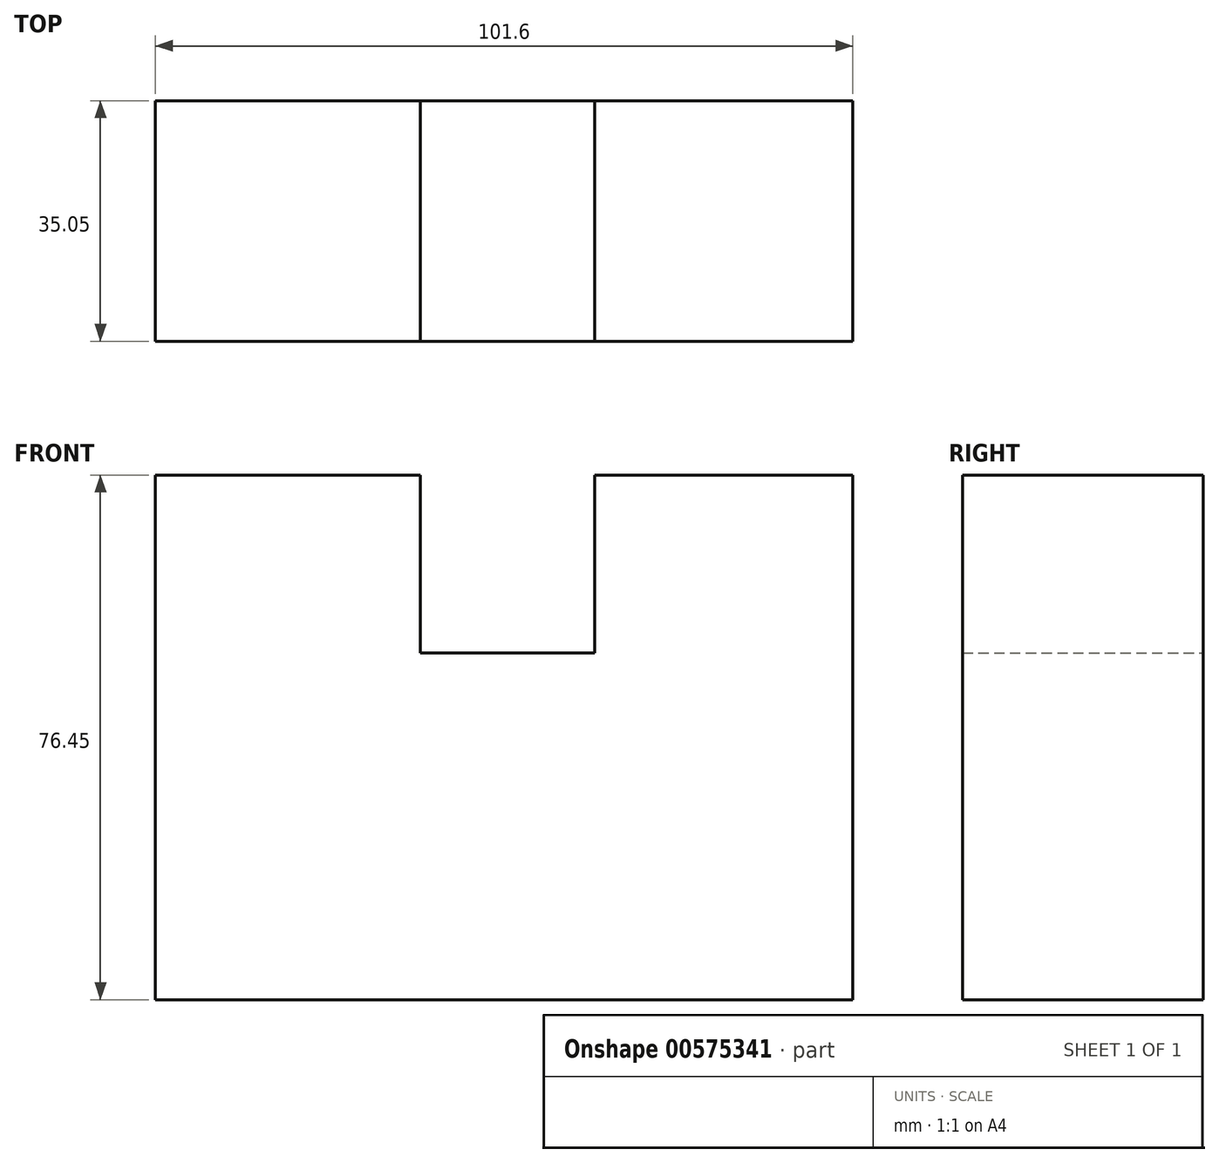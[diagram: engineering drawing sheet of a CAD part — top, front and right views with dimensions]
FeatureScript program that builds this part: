
annotation { "Feature Type Name" : "Feature", "Feature Type Description" : "" }
export const myFeature = defineFeature(function(context is Context, id is Id, definition is map)
    precondition{}
    {
        {
            var Q0;
            Q0=qCreatedBy(makeId("Front.planeOp"),FACE);
            var sketch = newSketch(context, id + "F0", { "sketchPlane" : qUnion([Q0])});
            skLineSegment(sketch, "E0", {"start": v(0, 0) * mm, "end": v(101.6, 0) * mm});
            skLineSegment(sketch, "E1", {"start": v(101.6, 0) * mm, "end": v(101.6, 76.45) * mm});
            skLineSegment(sketch, "E2", {"start": v(101.6, 76.45) * mm, "end": v(64, 76.45) * mm});
            skLineSegment(sketch, "E3", {"start": v(64, 76.45) * mm, "end": v(64, 50.55) * mm});
            skLineSegment(sketch, "E4", {"start": v(64, 50.55) * mm, "end": v(38.6, 50.55) * mm});
            skLineSegment(sketch, "E5", {"start": v(38.6, 50.55) * mm, "end": v(38.6, 76.45) * mm});
            skLineSegment(sketch, "E6", {"start": v(38.6, 76.45) * mm, "end": v(0, 76.45) * mm});
            skLineSegment(sketch, "E7", {"start": v(0, 76.45) * mm, "end": v(0, 0) * mm});
            skSolve(sketch);
        }
        {
            var Q0;
            Q0=makeQuery(id+"F0.imprint","IMPRINT",FACE,{"disambiguationData":[TD([[makeQuery(id+"F0.imprint","IMPRINT",EDGE,{"derivedFrom":sQuery(id+"F0.wireOp",EDGE,"E0")}),1.0]])]});
            extrude(context, id + "F1", {"entities" : qUnion([Q0]), "depth" : 35.05 * mm, "offsetDistance" : 25.4 * mm});
        }
        {
            var Q0;
            Q0=makeQuery(id+"F1.opExtrude","SWEPT_FACE",FACE,{"disambiguationData":[OSD([sQuery(id+"F0.wireOp",EDGE,"E6")])]});
            var Q1;
            Q1=makeQuery(id+"F1.opExtrude","SWEPT_FACE",FACE,{"disambiguationData":[OSD([sQuery(id+"F0.wireOp",EDGE,"E2")])]});
            extrude(context, id + "F2", {"entities" : qUnion([Q0, Q1]), "operationType" : NewBodyOperationType.ADD, "oppositeDirection" : true, "depth" : 1.02 * mm, "offsetDistance" : 25.4 * mm});
        }
        {
            var Q0;
            Q0=makeQuery(id+"F1.opExtrude","SWEPT_FACE",FACE,{"disambiguationData":[OSD([sQuery(id+"F0.wireOp",EDGE,"E6")])]});
            var sketch = newSketch(context, id + "F3", { "sketchPlane" : qUnion([Q0])});
            skLineSegment(sketch, "E8", {"start": v(354.06, -101.6) * mm, "end": v(354.06, 0) * mm});
            skLineSegment(sketch, "E9", {"start": v(354.06, -101.6) * mm, "end": v(444.54, -101.6) * mm});
            skLineSegment(sketch, "E10", {"start": v(444.54, -101.6) * mm, "end": v(444.54, -47.33) * mm});
            skLineSegment(sketch, "E11", {"start": v(354.06, 0) * mm, "end": v(468.6, 0) * mm});
            skLineSegment(sketch, "E12", {"start": v(468.6, 0) * mm, "end": v(522.47, 0) * mm});
            skLineSegment(sketch, "E13", {"start": v(522.47, 0) * mm, "end": v(531.12, -47.33) * mm});
            skLineSegment(sketch, "E14", {"start": v(531.12, -47.33) * mm, "end": v(444.54, -47.33) * mm});
            skSolve(sketch);
        }
        {
            var Q0;
            Q0 = qSketchRegion(id + "F3", true);
            extrude(context, id + "F4", {"entities" : qUnion([Q0]), "oppositeDirection" : true, "depth" : 91.95 * mm, "offsetDistance" : 25.4 * mm});
        }
        {
            var Q0;
            Q0=makeQuery(id+"F4.opExtrude","SWEPT_BODY",BODY,{"disambiguationData":[OSD([sQuery(id+"F3.wireOp",EDGE,"E8"),sQuery(id+"F3.wireOp",EDGE,"E9"),sQuery(id+"F3.wireOp",EDGE,"E10"),sQuery(id+"F3.wireOp",EDGE,"E11"),sQuery(id+"F3.wireOp",EDGE,"E12"),sQuery(id+"F3.wireOp",EDGE,"E13"),sQuery(id+"F3.wireOp",EDGE,"E14")])]});
            deleteBodies(context, id + "F5", {"entities" : qUnion([Q0])});
        }
    });
